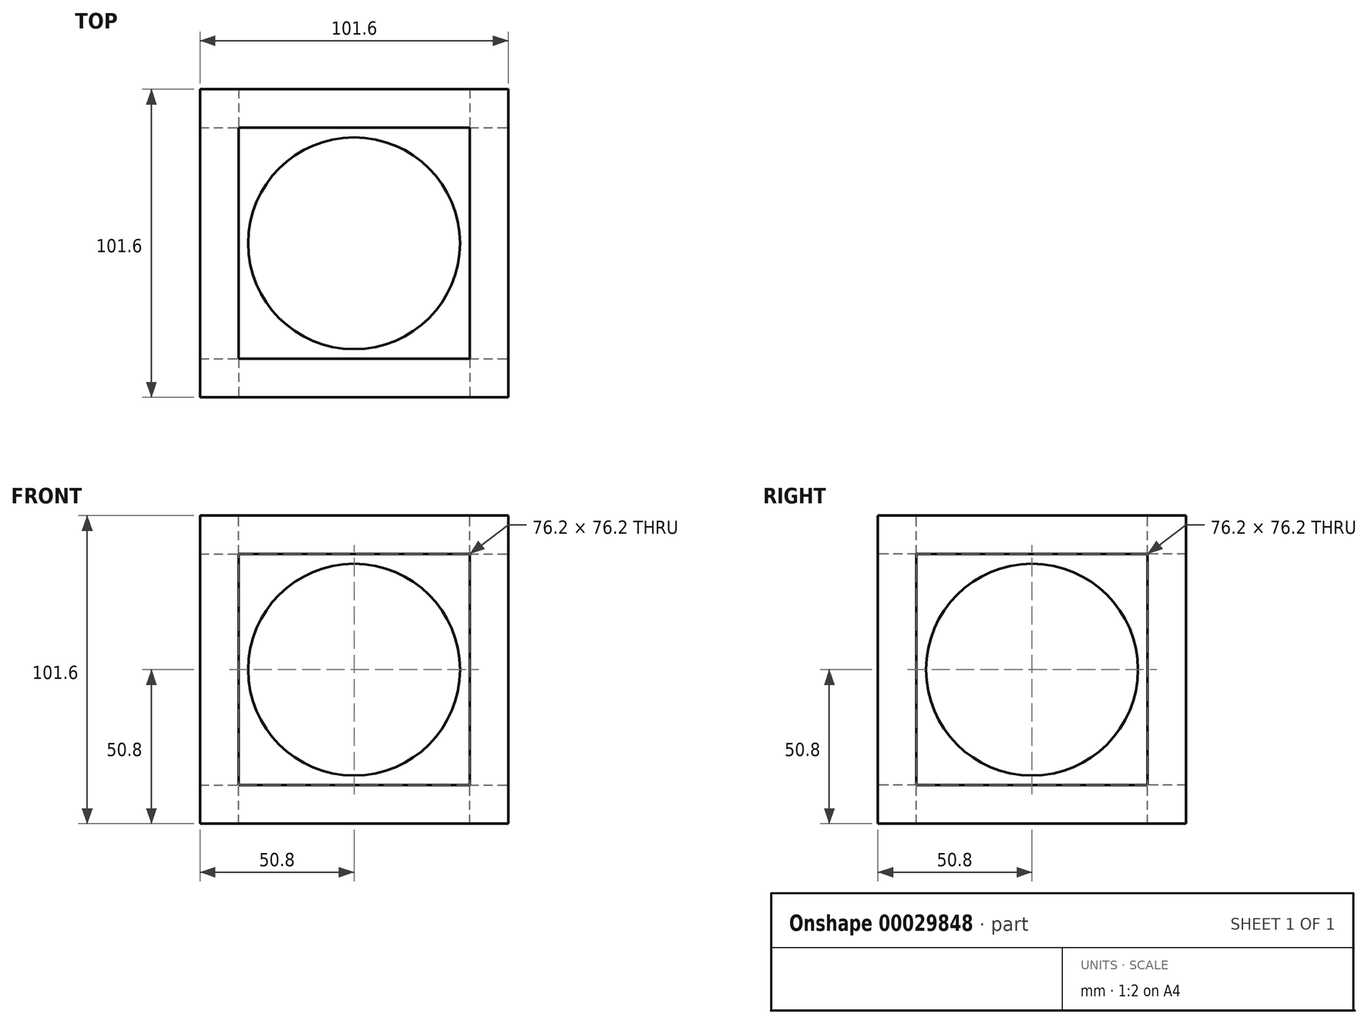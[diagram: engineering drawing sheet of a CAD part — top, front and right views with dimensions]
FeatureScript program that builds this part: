
annotation { "Feature Type Name" : "Feature", "Feature Type Description" : "" }
export const myFeature = defineFeature(function(context is Context, id is Id, definition is map)
    precondition{}
    {
        {
            var Q0;
            Q0=qCreatedBy(makeId("Front.planeOp"),FACE);
            var sketch = newSketch(context, id + "F0", { "sketchPlane" : qUnion([Q0])});
            skLineSegment(sketch, "E0.rect.bottom", {"start": v(50.8, -50.8) * mm, "end": v(-50.8, -50.8) * mm});
            skLineSegment(sketch, "E0.rect.top", {"start": v(50.8, 50.8) * mm, "end": v(-50.8, 50.8) * mm});
            skLineSegment(sketch, "E0.rect.left", {"start": v(50.8, -50.8) * mm, "end": v(50.8, 50.8) * mm});
            skLineSegment(sketch, "E0.rect.right", {"start": v(-50.8, -50.8) * mm, "end": v(-50.8, 50.8) * mm});
            skPoint(sketch, "E0.rect.middle", {"position": v(0, 0) * mm});
            skSolve(sketch);
        }
        {
            var Q0;
            Q0 = qSketchRegion(id + "F0", true);
            extrude(context, id + "F1", {"entities" : qUnion([Q0]), "depth" : 101.6 * mm});
        }
        {
            var Q0;
            Q0=makeQuery(id+"F1.opExtrude","SWEPT_FACE",FACE,{"disambiguationData":[OSD([sQuery(id+"F0.wireOp",EDGE,"E0.rect.top")])]});
            var sketch = newSketch(context, id + "F2", { "sketchPlane" : qUnion([Q0])});
            skLineSegment(sketch, "E1.0", {"start": v(38.1, -12.7) * mm, "end": v(-38.1, -12.7) * mm});
            skLineSegment(sketch, "E1.1", {"start": v(38.1, -88.9) * mm, "end": v(38.1, -12.7) * mm});
            skLineSegment(sketch, "E1.2", {"start": v(-38.1, -88.9) * mm, "end": v(38.1, -88.9) * mm});
            skLineSegment(sketch, "E1.3", {"start": v(-38.1, -12.7) * mm, "end": v(-38.1, -88.9) * mm});
            skSolve(sketch);
        }
        {
            var Q0;
            Q0=makeQuery(id+"F2.imprint","IMPRINT",FACE,{"disambiguationData":[TD([[makeQuery(id+"F2.imprint","IMPRINT",EDGE,{"derivedFrom":sQuery(id+"F2.wireOp",EDGE,"E1.0")}),1.0]])]});
            extrude(context, id + "F3", {"entities" : qUnion([Q0]), "operationType" : NewBodyOperationType.REMOVE, "oppositeDirection" : true, "depth" : 101.6 * mm});
        }
        {
            var Q0;
            Q0=makeQuery(id+"F1.opExtrude","SWEPT_FACE",FACE,{"disambiguationData":[OSD([sQuery(id+"F0.wireOp",EDGE,"E0.rect.left")])]});
            var sketch = newSketch(context, id + "F4", { "sketchPlane" : qUnion([Q0])});
            skLineSegment(sketch, "E2.0", {"start": v(-12.7, -38.1) * mm, "end": v(-12.7, 38.1) * mm});
            skLineSegment(sketch, "E2.1", {"start": v(-88.9, -38.1) * mm, "end": v(-12.7, -38.1) * mm});
            skLineSegment(sketch, "E2.2", {"start": v(-88.9, 38.1) * mm, "end": v(-88.9, -38.1) * mm});
            skLineSegment(sketch, "E2.3", {"start": v(-12.7, 38.1) * mm, "end": v(-88.9, 38.1) * mm});
            skSolve(sketch);
        }
        {
            var Q0;
            Q0=makeQuery(id+"F4.imprint","IMPRINT",FACE,{"disambiguationData":[TD([[makeQuery(id+"F4.imprint","IMPRINT",EDGE,{"derivedFrom":sQuery(id+"F4.wireOp",EDGE,"E2.0")}),1.0]])]});
            extrude(context, id + "F5", {"entities" : qUnion([Q0]), "operationType" : NewBodyOperationType.REMOVE, "oppositeDirection" : true, "depth" : 101.6 * mm});
        }
        {
            var Q0;
            Q0=makeQuery(id+"F1.opExtrude","CAP_FACE",FACE,{"disambiguationData":[OSD([sQuery(id+"F0.wireOp",EDGE,"E0.rect.bottom"),sQuery(id+"F0.wireOp",EDGE,"E0.rect.top"),sQuery(id+"F0.wireOp",EDGE,"E0.rect.left"),sQuery(id+"F0.wireOp",EDGE,"E0.rect.right")])],"isStart":false});
            var sketch = newSketch(context, id + "F6", { "sketchPlane" : qUnion([Q0])});
            skLineSegment(sketch, "E3.0", {"start": v(-38.1, -38.1) * mm, "end": v(38.1, -38.1) * mm});
            skLineSegment(sketch, "E3.1", {"start": v(-38.1, 38.1) * mm, "end": v(-38.1, -38.1) * mm});
            skLineSegment(sketch, "E3.2", {"start": v(38.1, 38.1) * mm, "end": v(-38.1, 38.1) * mm});
            skLineSegment(sketch, "E3.3", {"start": v(38.1, -38.1) * mm, "end": v(38.1, 38.1) * mm});
            skSolve(sketch);
        }
        {
            var Q0;
            Q0=makeQuery(id+"F6.imprint","IMPRINT",FACE,{"disambiguationData":[TD([[makeQuery(id+"F6.imprint","IMPRINT",EDGE,{"derivedFrom":sQuery(id+"F6.wireOp",EDGE,"E3.0")}),1.0]])]});
            extrude(context, id + "F7", {"entities" : qUnion([Q0]), "operationType" : NewBodyOperationType.REMOVE, "oppositeDirection" : true, "depth" : 101.6 * mm});
        }
        {
            var Q0;
            Q0=makeQuery(id+"F1.opExtrude","CAP_FACE",FACE,{"disambiguationData":[OSD([sQuery(id+"F0.wireOp",EDGE,"E0.rect.bottom"),sQuery(id+"F0.wireOp",EDGE,"E0.rect.top"),sQuery(id+"F0.wireOp",EDGE,"E0.rect.left"),sQuery(id+"F0.wireOp",EDGE,"E0.rect.right")])],"isStart":false});
            cPlane(context, id + "F8", {"entities" : qUnion([Q0]), "cplaneType" : CPlaneType.OFFSET, "offset" : 50.8 * mm, "oppositeDirection" : true, "width" : 152.4 * mm, "height" : 152.4 * mm});
        }
        {
            var Q0;
            Q0=qCreatedBy(id+"F8.planeOp",FACE);
            var sketch = newSketch(context, id + "F9", { "sketchPlane" : qUnion([Q0])});
            skCircle(sketch, "E4", {"center": v(0, 0) * mm, "radius": 34.93 * mm});
            skLineSegment(sketch, "E5", {"start": v(0, -34.93) * mm, "end": v(0, 34.93) * mm});
            skSolve(sketch);
        }
        {
            var Q0;
            {var subQ0=sQuery(id+"F9.wireOp",EDGE,"E5");Q0=makeQuery(id+"F9.imprint","IMPRINT",FACE,{"disambiguationData":[TD([[makeQuery(id+"F9.imprint","IMPRINT",EDGE,{"derivedFrom":subQ0}),-1.0]])]});}
            var Q1;
            Q1=sQuery(id+"F9.wireOp",EDGE,"E5");
            revolve(context, id + "F10", {"entities" : qUnion([Q0]), "axis" : qUnion([Q1]), "revolveType" : RevolveType.FULL});
        }
    });
